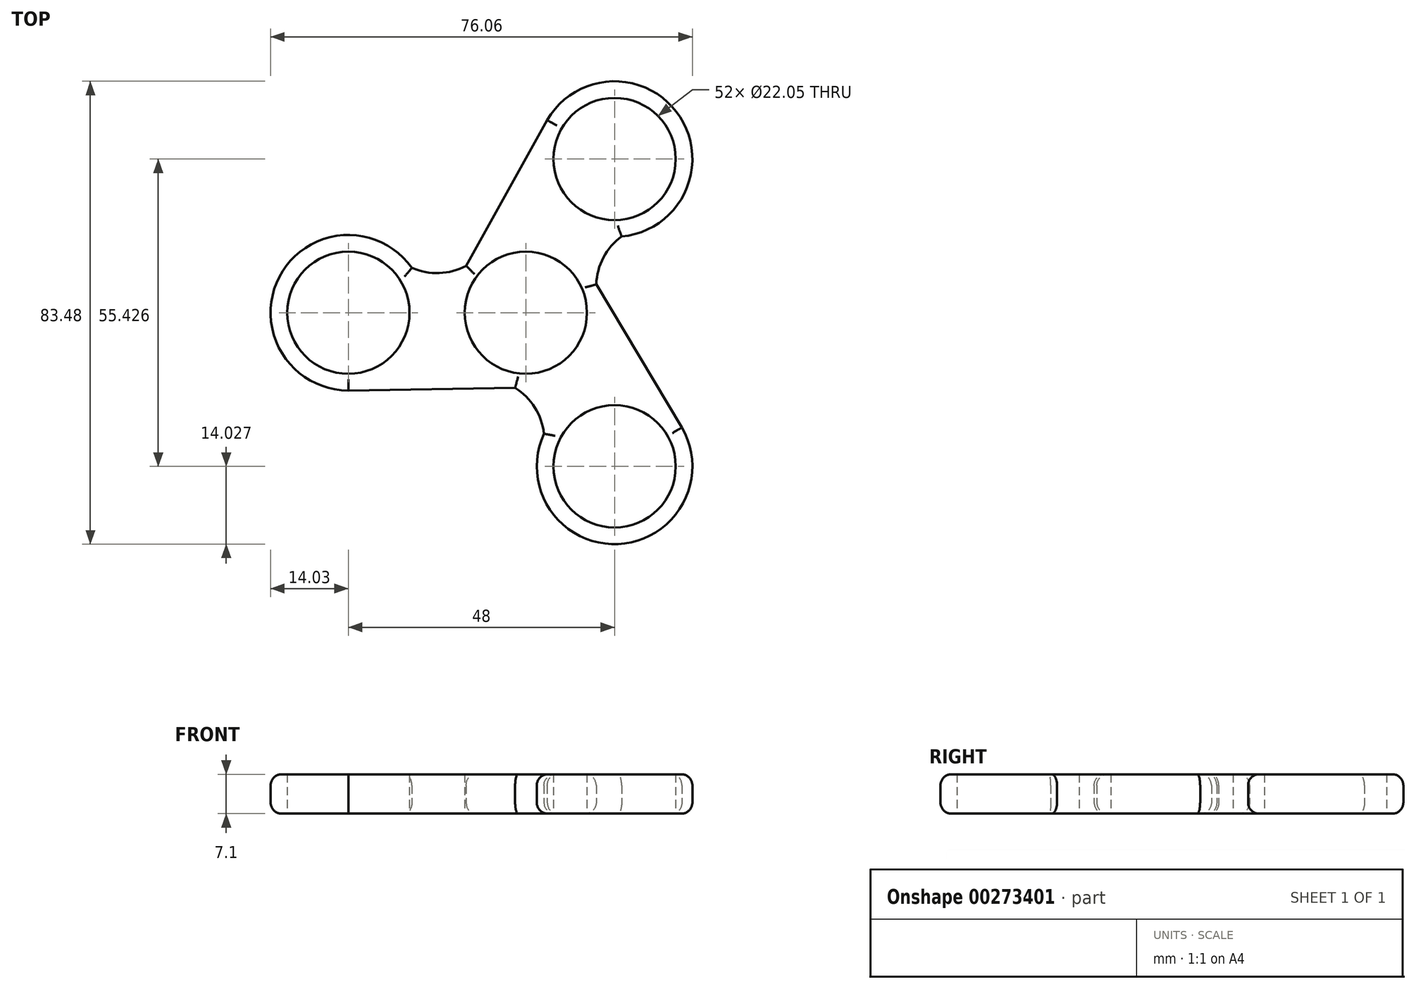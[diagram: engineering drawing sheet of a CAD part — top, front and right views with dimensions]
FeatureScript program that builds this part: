
annotation { "Feature Type Name" : "Feature", "Feature Type Description" : "" }
export const myFeature = defineFeature(function(context is Context, id is Id, definition is map)
    precondition{}
    {
        {
            var Q0;
            Q0=qCreatedBy(makeId("Top.planeOp"),FACE);
            var sketch = newSketch(context, id + "F0", { "sketchPlane" : qUnion([Q0])});
            skCircle(sketch, "E0", {"center": v(0, 0) * mm, "radius": 11.03 * mm});
            skCircle(sketch, "E1", {"center": v(16, 27.71) * mm, "radius": 11.03 * mm});
            skLineSegment(sketch, "E2", {"start": v(0, 0) * mm, "end": v(16, 27.71) * mm, "construction": true});
            skArc(sketch, "E3", {"start": v(17.28, 13.75) * mm, "mid": v(27.81, 35.27) * mm, "end": v(3.85, 34.73) * mm});
            skLineSegment(sketch, "E4", {"start": v(16, 27.71) * mm, "end": v(3.85, 34.73) * mm, "construction": true});
            skPoint(sketch, "E5.visualSharp", {"position": v(8.99, 15.57) * mm});
            skLineSegment(sketch, "E6", {"start": v(16, 27.71) * mm, "end": v(28.15, 20.7) * mm, "construction": true});
            skLineSegment(sketch, "E7", {"start": v(8, 13.86) * mm, "end": v(-1.53, 19.36) * mm, "construction": true});
            skArc(sketch, "E8", {"start": v(2.29, 25.96) * mm, "mid": v(3.75, 21.3) * mm, "end": v(6.74, 17.44) * mm});
            skLineSegment(sketch, "E9", {"start": v(12.33, 11.36) * mm, "end": v(15.11, 14.17) * mm, "construction": true});
            skLineSegment(sketch, "E10", {"start": v(12.33, 11.36) * mm, "end": v(10.43, 8.07) * mm, "construction": true});
            skCircle(sketch, "E11", {"center": v(0, 0) * mm, "radius": 13.19 * mm, "construction": true});
            skArc(sketch, "E12", {"start": v(10.22, 8.37) * mm, "mid": v(5.28, 12.63) * mm, "end": v(-1.08, 14.1) * mm});
            skPoint(sketch, "E13.center", {"position": v(-0.23, 0.06) * mm});
            skLineSegment(sketch, "E14", {"start": v(6.74, 17.44) * mm, "end": v(-3.41, 15.54) * mm});
            skPoint(sketch, "E15.orphan", {"position": v(-4.4, 14.37) * mm});
            skPoint(sketch, "E16.orphan", {"position": v(14.14, -3.77) * mm});
            skPoint(sketch, "E17.orphan", {"position": v(15.29, -4.48) * mm});
            skPoint(sketch, "E18.orphan", {"position": v(9.2, 15.94) * mm});
            skArc(sketch, "E19.1.1", {"start": v(-23.63, -11) * mm, "mid": v(-20.32, -7.4) * mm, "end": v(-18.48, -2.88) * mm});
            skLineSegment(sketch, "E19.1.2", {"start": v(-32, 0) * mm, "end": v(-32, 14.03) * mm, "construction": true});
            skPoint(sketch, "E19.1.4", {"position": v(-18.4, 0) * mm});
            skPoint(sketch, "E19.1.5", {"position": v(0.06, -0.23) * mm});
            skPoint(sketch, "E19.1.6", {"position": v(-10.25, -11) * mm});
            skCircle(sketch, "E19.1.7", {"center": v(-32, 0) * mm, "radius": 11.03 * mm});
            skLineSegment(sketch, "E19.1.8", {"start": v(-18.48, -2.88) * mm, "end": v(-11.75, -10.73) * mm});
            skLineSegment(sketch, "E19.1.9", {"start": v(-16, 0) * mm, "end": v(-16, -11) * mm, "construction": true});
            skPoint(sketch, "E19.1.10", {"position": v(-17.97, 0) * mm});
            skArc(sketch, "E19.1.12", {"start": v(-12.36, 4.67) * mm, "mid": v(-13.58, -1.75) * mm, "end": v(-11.67, -7.99) * mm});
            skArc(sketch, "E19.1.13", {"start": v(-20.54, 8.09) * mm, "mid": v(-44.45, 6.45) * mm, "end": v(-32, -14.02) * mm});
            skLineSegment(sketch, "E19.1.14", {"start": v(-32, 0) * mm, "end": v(-32, -14.02) * mm, "construction": true});
            skLineSegment(sketch, "E19.1.16", {"start": v(-16, 5) * mm, "end": v(-12.2, 5) * mm, "construction": true});
            skLineSegment(sketch, "E19.1.18", {"start": v(-16, 5) * mm, "end": v(-19.8, 6) * mm, "construction": true});
            skArc(sketch, "E19.2.1", {"start": v(21.34, -14.96) * mm, "mid": v(16.57, -13.9) * mm, "end": v(11.73, -14.56) * mm});
            skLineSegment(sketch, "E19.2.2", {"start": v(16, -27.71) * mm, "end": v(3.85, -34.73) * mm, "construction": true});
            skPoint(sketch, "E19.2.4", {"position": v(9.2, -15.94) * mm});
            skPoint(sketch, "E19.2.5", {"position": v(0.17, 0.17) * mm});
            skPoint(sketch, "E19.2.6", {"position": v(14.65, -3.37) * mm});
            skCircle(sketch, "E19.2.7", {"center": v(16, -27.71) * mm, "radius": 11.03 * mm});
            skLineSegment(sketch, "E19.2.8", {"start": v(11.73, -14.56) * mm, "end": v(15.17, -4.82) * mm});
            skLineSegment(sketch, "E19.2.9", {"start": v(8, -13.86) * mm, "end": v(17.53, -8.36) * mm, "construction": true});
            skPoint(sketch, "E19.2.10", {"position": v(8.99, -15.57) * mm});
            skArc(sketch, "E19.2.12", {"start": v(2.14, -13.04) * mm, "mid": v(8.3, -10.89) * mm, "end": v(12.75, -6.11) * mm});
            skArc(sketch, "E19.2.13", {"start": v(3.27, -21.83) * mm, "mid": v(16.64, -41.72) * mm, "end": v(28.15, -20.7) * mm});
            skLineSegment(sketch, "E19.2.14", {"start": v(16, -27.71) * mm, "end": v(28.15, -20.7) * mm, "construction": true});
            skLineSegment(sketch, "E19.2.16", {"start": v(3.67, -16.36) * mm, "end": v(1.77, -13.07) * mm, "construction": true});
            skLineSegment(sketch, "E19.2.18", {"start": v(3.67, -16.36) * mm, "end": v(4.7, -20.15) * mm, "construction": true});
            skArc(sketch, "E20.0", {"start": v(13.95, 14.45) * mm, "mid": v(11.63, 11.7) * mm, "end": v(10.22, 8.37) * mm});
            skArc(sketch, "E21.trimOffspring", {"start": v(9.86, 4.93) * mm, "mid": v(9.88, 4.6) * mm, "end": v(9.9, 4.28) * mm});
            skLineSegment(sketch, "E22", {"start": v(2.29, 25.96) * mm, "end": v(-3.41, 15.54) * mm});
            skLineSegment(sketch, "E23.1.0", {"start": v(-23.63, -11) * mm, "end": v(-11.75, -10.73) * mm});
            skArc(sketch, "E23.1.1", {"start": v(-19.5, 4.86) * mm, "mid": v(-15.94, 4.22) * mm, "end": v(-12.36, 4.67) * mm});
            skLineSegment(sketch, "E23.2.0", {"start": v(21.34, -14.96) * mm, "end": v(15.17, -4.82) * mm});
            skArc(sketch, "E23.2.1", {"start": v(5.54, -19.3) * mm, "mid": v(4.32, -15.92) * mm, "end": v(2.14, -13.04) * mm});
            skPoint(sketch, "E24.orphan", {"position": v(-11.52, -11) * mm});
            skArc(sketch, "E25", {"start": v(13.95, 14.45) * mm, "mid": v(6.42, 14.96) * mm, "end": v(-1.08, 14.1) * mm});
            skPoint(sketch, "E26.orphan", {"position": v(-1.86, 14.06) * mm});
            skArc(sketch, "E27.1.0", {"start": v(-19.5, 4.86) * mm, "mid": v(-16.17, -1.92) * mm, "end": v(-11.67, -7.99) * mm});
            skArc(sketch, "E27.2.0", {"start": v(5.54, -19.3) * mm, "mid": v(9.75, -13.04) * mm, "end": v(12.75, -6.11) * mm});
            skPoint(sketch, "E28.orphan", {"position": v(13.07, -5.5) * mm});
            skPoint(sketch, "E29.orphan", {"position": v(-11.3, -8.57) * mm});
            skArc(sketch, "E30", {"start": v(17.28, 13.75) * mm, "mid": v(14, 9.94) * mm, "end": v(12.7, 5.1) * mm});
            skPoint(sketch, "E31.orphan", {"position": v(12.4, 4.52) * mm});
            skLineSegment(sketch, "E32", {"start": v(3.85, 34.73) * mm, "end": v(-10.76, 8.44) * mm});
            skPoint(sketch, "E33.orphan", {"position": v(-10.1, 8.47) * mm});
            skLineSegment(sketch, "E34.1.0", {"start": v(-32, -14.02) * mm, "end": v(-1.93, -13.54) * mm});
            skArc(sketch, "E34.1.1", {"start": v(-20.54, 8.09) * mm, "mid": v(-15.61, 7.15) * mm, "end": v(-10.76, 8.44) * mm});
            skLineSegment(sketch, "E34.2.0", {"start": v(28.15, -20.7) * mm, "end": v(12.7, 5.1) * mm});
            skArc(sketch, "E34.2.1", {"start": v(3.27, -21.83) * mm, "mid": v(1.61, -17.1) * mm, "end": v(-1.93, -13.54) * mm});
            skPoint(sketch, "E35.orphan", {"position": v(-11.08, 7.87) * mm});
            skPoint(sketch, "E36.orphan", {"position": v(-9.83, 9) * mm});
            skPoint(sketch, "E37.orphan", {"position": v(3.27, -21.83) * mm});
            skPoint(sketch, "E38.orphan", {"position": v(-2.87, -13.01) * mm});
            skPoint(sketch, "E39.orphan", {"position": v(-1.27, -13.53) * mm});
            skPoint(sketch, "E40.orphan", {"position": v(12.35, 5.66) * mm});
            skPoint(sketch, "E41.orphan", {"position": v(12.7, 4.02) * mm});
            skPoint(sketch, "E42.orphan", {"position": v(-3.77, 15.48) * mm});
            skSolve(sketch);
        }
        {
            var Q0;
            Q0=makeQuery(id+"F0.imprint","IMPRINT",FACE,{"disambiguationData":[TD([[makeQuery(id+"F0.imprint","IMPRINT",EDGE,{"derivedFrom":sQuery(id+"F0.wireOp",EDGE,"ea44153e-c5e4-4200-878d-53ebf284e07f.1.0")}),-1.0]])]});
            var Q1;
            Q1=makeQuery(id+"F0.imprint","IMPRINT",FACE,{"disambiguationData":[TD([[makeQuery(id+"F0.imprint","IMPRINT",EDGE,{"derivedFrom":sQuery(id+"F0.wireOp",EDGE,"E0")}),-1.0]])]});
            var Q2;
            Q2=makeQuery(id+"F0.imprint","IMPRINT",FACE,{"disambiguationData":[TD([[makeQuery(id+"F0.imprint","IMPRINT",EDGE,{"derivedFrom":sQuery(id+"F0.wireOp",EDGE,"E1")}),-1.0]])]});
            var Q3;
            {var subQ0=sQuery(id+"F0.wireOp",EDGE,"zqQpl2xC-KShR-byGl-JfGq-b1LpVGurQPJH");Q3=makeQuery(id+"F0.imprint","IMPRINT",FACE,{"disambiguationData":[TD([[makeQuery(id+"F0.imprint","IMPRINT",EDGE,{"derivedFrom":subQ0}),-1.0]])]});}
            var Q4;
            Q4=makeQuery(id+"F0.imprint","IMPRINT",FACE,{"disambiguationData":[TD([[makeQuery(id+"F0.imprint","IMPRINT",EDGE,{"derivedFrom":sQuery(id+"F0.wireOp",EDGE,"E19.1.12")}),-1.0]])]});
            var Q5;
            Q5=makeQuery(id+"F0.imprint","IMPRINT",FACE,{"disambiguationData":[TD([[makeQuery(id+"F0.imprint","IMPRINT",EDGE,{"derivedFrom":sQuery(id+"F0.wireOp",EDGE,"E19.1.1")}),-1.0]])]});
            var Q6;
            Q6=makeQuery(id+"F0.imprint","IMPRINT",FACE,{"disambiguationData":[TD([[makeQuery(id+"F0.imprint","IMPRINT",EDGE,{"derivedFrom":sQuery(id+"F0.wireOp",EDGE,"E8")}),-1.0]])]});
            var Q7;
            Q7=makeQuery(id+"F0.imprint","IMPRINT",FACE,{"disambiguationData":[TD([[makeQuery(id+"F0.imprint","IMPRINT",EDGE,{"derivedFrom":sQuery(id+"F0.wireOp",EDGE,"E12")}),-1.0]])]});
            var Q8;
            Q8=makeQuery(id+"F0.imprint","IMPRINT",FACE,{"disambiguationData":[TD([[makeQuery(id+"F0.imprint","IMPRINT",EDGE,{"derivedFrom":sQuery(id+"F0.wireOp",EDGE,"E19.2.1")}),-1.0]])]});
            var Q9;
            Q9=makeQuery(id+"F0.imprint","IMPRINT",FACE,{"disambiguationData":[TD([[makeQuery(id+"F0.imprint","IMPRINT",EDGE,{"derivedFrom":sQuery(id+"F0.wireOp",EDGE,"E19.2.12")}),-1.0]])]});
            extrude(context, id + "F1", {"entities" : qUnion([Q0, Q1, Q2, Q3, Q4, Q5, Q6, Q7, Q8, Q9]), "depth" : 7.1 * mm});
        }
        {
            var Q0;
            Q0=makeQuery(id+"F1.opExtrude","CAP_EDGE",EDGE,{"disambiguationData":[OSD([sQuery(id+"F0.wireOp",EDGE,"E34.1.1")])],"isStart":false});
            var Q1;
            Q1=makeQuery(id+"F1.opExtrude","CAP_EDGE",EDGE,{"disambiguationData":[OSD([sQuery(id+"F0.wireOp",EDGE,"E32")])],"isStart":false});
            var Q2;
            Q2=makeQuery(id+"F1.opExtrude","CAP_EDGE",EDGE,{"disambiguationData":[OSD([sQuery(id+"F0.wireOp",EDGE,"E3")])],"isStart":false});
            var Q3;
            Q3=makeQuery(id+"F1.opExtrude","CAP_EDGE",EDGE,{"disambiguationData":[OSD([sQuery(id+"F0.wireOp",EDGE,"E30")])],"isStart":false});
            var Q4;
            Q4=makeQuery(id+"F1.opExtrude","CAP_EDGE",EDGE,{"disambiguationData":[OSD([sQuery(id+"F0.wireOp",EDGE,"E34.2.0")])],"isStart":false});
            var Q5;
            Q5=makeQuery(id+"F1.opExtrude","CAP_EDGE",EDGE,{"disambiguationData":[OSD([sQuery(id+"F0.wireOp",EDGE,"E19.2.13")])],"isStart":false});
            var Q6;
            Q6=makeQuery(id+"F1.opExtrude","CAP_EDGE",EDGE,{"disambiguationData":[OSD([sQuery(id+"F0.wireOp",EDGE,"E34.2.1")])],"isStart":false});
            var Q7;
            Q7=makeQuery(id+"F1.opExtrude","CAP_EDGE",EDGE,{"disambiguationData":[OSD([sQuery(id+"F0.wireOp",EDGE,"E34.1.0")])],"isStart":false});
            var Q8;
            Q8=makeQuery(id+"F1.opExtrude","CAP_EDGE",EDGE,{"disambiguationData":[OSD([sQuery(id+"F0.wireOp",EDGE,"E19.1.13")])],"isStart":false});
            var Q9;
            Q9=makeQuery(id+"F1.opExtrude","CAP_EDGE",EDGE,{"disambiguationData":[OSD([sQuery(id+"F0.wireOp",EDGE,"E34.1.0")])],"isStart":true});
            var Q10;
            Q10=makeQuery(id+"F1.opExtrude","CAP_EDGE",EDGE,{"disambiguationData":[OSD([sQuery(id+"F0.wireOp",EDGE,"E34.2.1")])],"isStart":true});
            var Q11;
            Q11=makeQuery(id+"F1.opExtrude","CAP_EDGE",EDGE,{"disambiguationData":[OSD([sQuery(id+"F0.wireOp",EDGE,"E19.2.13")])],"isStart":true});
            var Q12;
            Q12=makeQuery(id+"F1.opExtrude","CAP_EDGE",EDGE,{"disambiguationData":[OSD([sQuery(id+"F0.wireOp",EDGE,"E34.2.0")])],"isStart":true});
            var Q13;
            Q13=makeQuery(id+"F1.opExtrude","CAP_EDGE",EDGE,{"disambiguationData":[OSD([sQuery(id+"F0.wireOp",EDGE,"E30")])],"isStart":true});
            var Q14;
            Q14=makeQuery(id+"F1.opExtrude","CAP_EDGE",EDGE,{"disambiguationData":[OSD([sQuery(id+"F0.wireOp",EDGE,"E3")])],"isStart":true});
            var Q15;
            Q15=makeQuery(id+"F1.opExtrude","CAP_EDGE",EDGE,{"disambiguationData":[OSD([sQuery(id+"F0.wireOp",EDGE,"E32")])],"isStart":true});
            var Q16;
            Q16=makeQuery(id+"F1.opExtrude","CAP_EDGE",EDGE,{"disambiguationData":[OSD([sQuery(id+"F0.wireOp",EDGE,"E34.1.1")])],"isStart":true});
            var Q17;
            Q17=makeQuery(id+"F1.opExtrude","CAP_EDGE",EDGE,{"disambiguationData":[OSD([sQuery(id+"F0.wireOp",EDGE,"E19.1.13")])],"isStart":true});
            fillet(context, id + "F2", {"entities" : qUnion([Q0, Q1, Q2, Q3, Q4, Q5, Q6, Q7, Q8, Q9, Q10, Q11, Q12, Q13, Q14, Q15, Q16, Q17]), "radius" : 2 * mm, "tangentPropagation" : true, "allowEdgeOverflow" : false});
        }
    });
